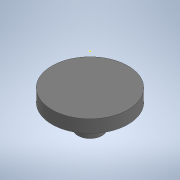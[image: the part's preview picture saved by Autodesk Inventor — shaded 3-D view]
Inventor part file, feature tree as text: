
AUTODESK INVENTOR PART (.ipt)
format: ipt  version: 2021.1 (Build 251245000, 245)  size: 198,656 bytes
history: native  units: in
note: dims shown in document units (in); Inventor stores cm internally (conversion verified against a paired STEP export)
features: sketch x8, extrude x7, other x2, revolve x1, mirror x1, reference x1
ambient origin geometry x8: Origin, YZ Plane, XZ Plane, XY Plane, X Axis, Y Axis, Z Axis, Center Point
bodies: Solid1 (feature_tree)
feature tree (20):
  revolve  "Revolution1"  [1 undecoded]
  extrude  "Extrusion1"  TaperAngle=90.0deg  [1 undecoded]
  extrude  "Extrusion3"  Depth=1.24in
  extrude  "Extrusion4"  Depth=0.5in TaperAngle=0.0deg
  extrude  "Extrusion5"  Depth=0.5in
  mirror  "Mirror1"
  extrude  "Extrusion6"  Depth=0.5in TaperAngle=0.0deg
  extrude  "Extrusion7"  Depth=0.75in TaperAngle=0.0deg
  sketch  "Sketch12"  dims[d28=0.875in d29=0.75in d30=0.0in]
  extrude  "Extrusion8"  TaperAngle=0.0deg  [1 undecoded]
  sketch  "Sketch5"  dims[d0=2.0in d1=0.1969in]
  sketch  "Sketch7"  dims[d2=0.4751in d6=90.0deg]
  sketch  "Sketch8"  dims[d13=1.4in d15=1.24in]
  sketch  "Sketch9"  dims[d16=0.6693in d17=0.5in d18=0.0in]
  reference  "Reference1"
  sketch  "Sketch10"  dims[d23=1.5in d24=0.5in]
  sketch  "Sketch11"  dims[d25=0.75in d26=0.5in d27=0.0in]
  sketch  "Sketch13"  dims[d31=0.39in d32=0.0in d33=0.0in d34=0.25in d35=0.0in d36=0.25in d37=0.0in d38=0.5in d39=1.5in d40=0.0in d41=0.0in]
  other  "ForkMountWithCelestronTubeConnector.iam"
  other  "6x3_8-keyedDriveShaft:2"
note: 3 required parameter values undecoded (feature->parameter linkage not recoverable at this tier; creation-order binding heuristic only, values carry confidence <= 0.55)